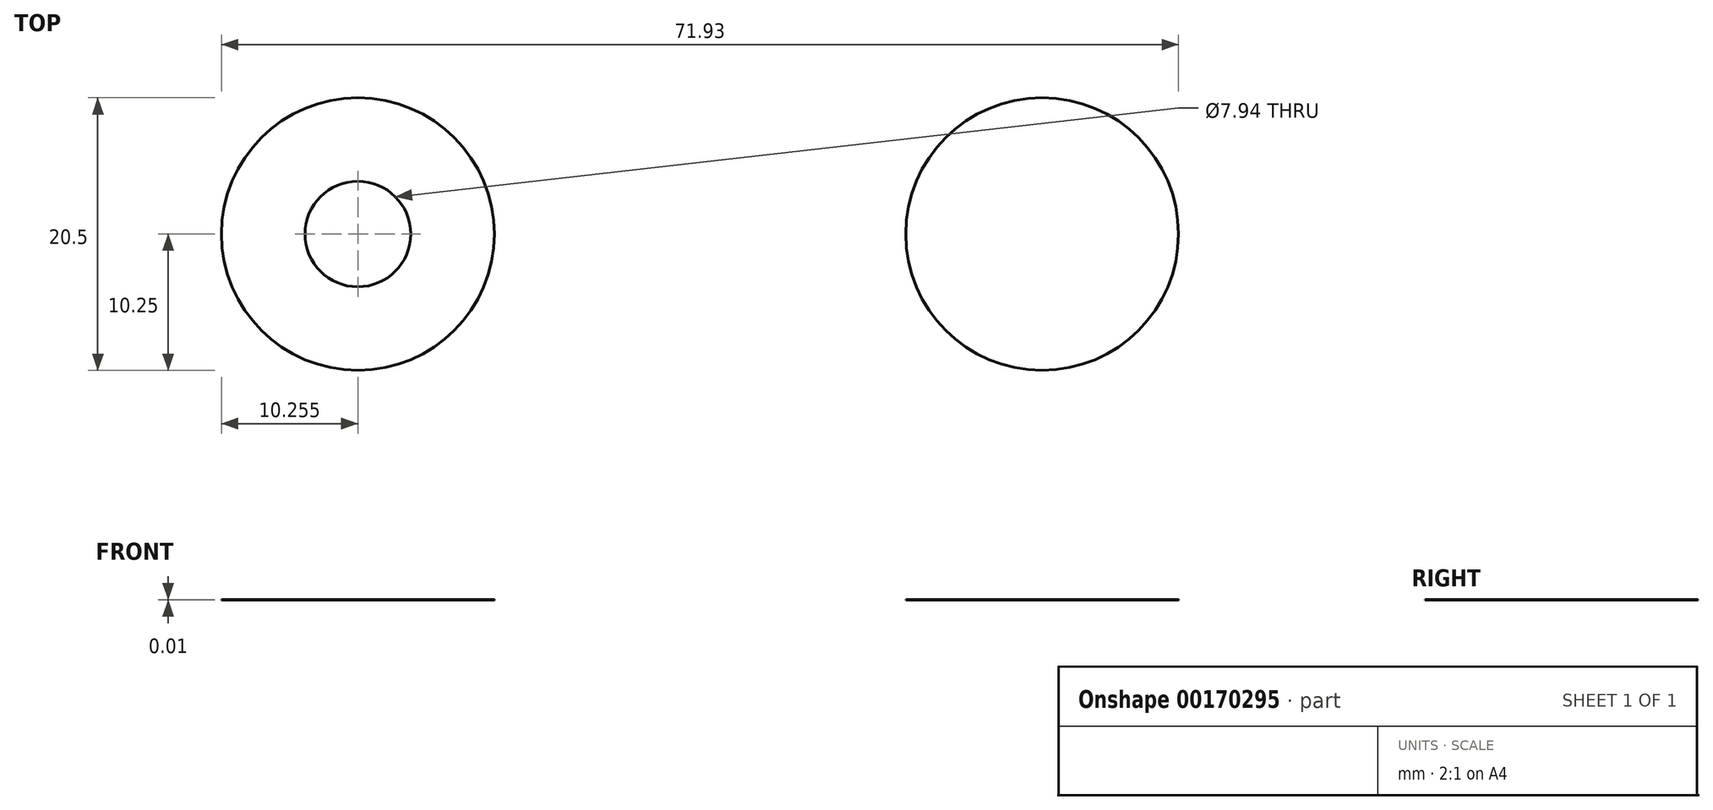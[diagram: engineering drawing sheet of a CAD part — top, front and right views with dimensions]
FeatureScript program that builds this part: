
annotation { "Feature Type Name" : "Feature", "Feature Type Description" : "" }
export const myFeature = defineFeature(function(context is Context, id is Id, definition is map)
    precondition{}
    {
        {
            var Q0;
            Q0=qCreatedBy(makeId("Top.planeOp"),FACE);
            var sketch = newSketch(context, id + "F0", { "sketchPlane" : qUnion([Q0])});
            skCircle(sketch, "E0", {"center": v(0, 0) * mm, "radius": 10.25 * mm});
            skCircle(sketch, "E1.MirrorC", {"center": v(23.76, 0) * mm, "radius": 10.25 * mm});
            skCircle(sketch, "E2", {"center": v(23.76, 0) * mm, "radius": 3.97 * mm});
            skCircle(sketch, "E3.MirrorC", {"center": v(-27.67, 0) * mm, "radius": 10.25 * mm});
            skCircle(sketch, "E4.MirrorC", {"center": v(-51.43, 0) * mm, "radius": 10.25 * mm});
            skCircle(sketch, "E5.MirrorC", {"center": v(-51.43, 0) * mm, "radius": 3.97 * mm});
            skSolve(sketch);
        }
        {
            var Q0;
            Q0=makeQuery(id+"F0.imprint","IMPRINT",FACE,{"disambiguationData":[TD([[makeQuery(id+"F0.imprint","IMPRINT",EDGE,{"derivedFrom":sQuery(id+"F0.wireOp",EDGE,"6cf06522-f0e1-4161-a4df-555c12732c2a0.MirrorC")}),1.0]])]});
            var Q1;
            Q1=makeQuery(id+"F0.imprint","IMPRINT",FACE,{"disambiguationData":[TD([[makeQuery(id+"F0.imprint","IMPRINT",EDGE,{"derivedFrom":sQuery(id+"F0.wireOp",EDGE,"62cb541d-35a7-4775-903f-eaa9cb58beb80.MirrorC")}),-1.0]])]});
            var Q2;
            Q2=makeQuery(id+"F0.imprint","IMPRINT",FACE,{"disambiguationData":[TD([[makeQuery(id+"F0.imprint","IMPRINT",EDGE,{"derivedFrom":sQuery(id+"F0.wireOp",EDGE,"E0")}),1.0]])]});
            var Q3;
            Q3=makeQuery(id+"F0.imprint","IMPRINT",FACE,{"disambiguationData":[TD([[makeQuery(id+"F0.imprint","IMPRINT",EDGE,{"derivedFrom":sQuery(id+"F0.wireOp",EDGE,"E3.MirrorC")}),-1.0]])]});
            extrude(context, id + "F1", {"entities" : qUnion([Q0, Q1, Q2, Q3]), "depth" : 3 / 203.2 * mm});
        }
        {
            var Q0;
            Q0=makeQuery(id+"F0.imprint","IMPRINT",FACE,{"disambiguationData":[TD([[makeQuery(id+"F0.imprint","IMPRINT",EDGE,{"derivedFrom":sQuery(id+"F0.wireOp",EDGE,"E4.MirrorC")}),1.0]])]});
            var Q1;
            Q1=makeQuery(id+"F0.imprint","IMPRINT",FACE,{"disambiguationData":[TD([[makeQuery(id+"F0.imprint","IMPRINT",EDGE,{"derivedFrom":sQuery(id+"F0.wireOp",EDGE,"ac182b1d-860f-4c9f-bdf6-42b0f8c41b820.MirrorC")}),-1.0]])]});
            var Q2;
            Q2=makeQuery(id+"F0.imprint","IMPRINT",FACE,{"disambiguationData":[TD([[makeQuery(id+"F0.imprint","IMPRINT",EDGE,{"derivedFrom":sQuery(id+"F0.wireOp",EDGE,"f7a2c4bc-eb25-4be7-a859-591a57d82fb10.MirrorC")}),1.0]])]});
            var Q3;
            Q3=makeQuery(id+"F0.imprint","IMPRINT",FACE,{"disambiguationData":[TD([[makeQuery(id+"F0.imprint","IMPRINT",EDGE,{"derivedFrom":sQuery(id+"F0.wireOp",EDGE,"E1.MirrorC")}),-1.0]])]});
            extrude(context, id + "F2", {"entities" : qUnion([Q0, Q1, Q2, Q3]), "depth" : 5 / 406.4 * mm});
        }
    });
